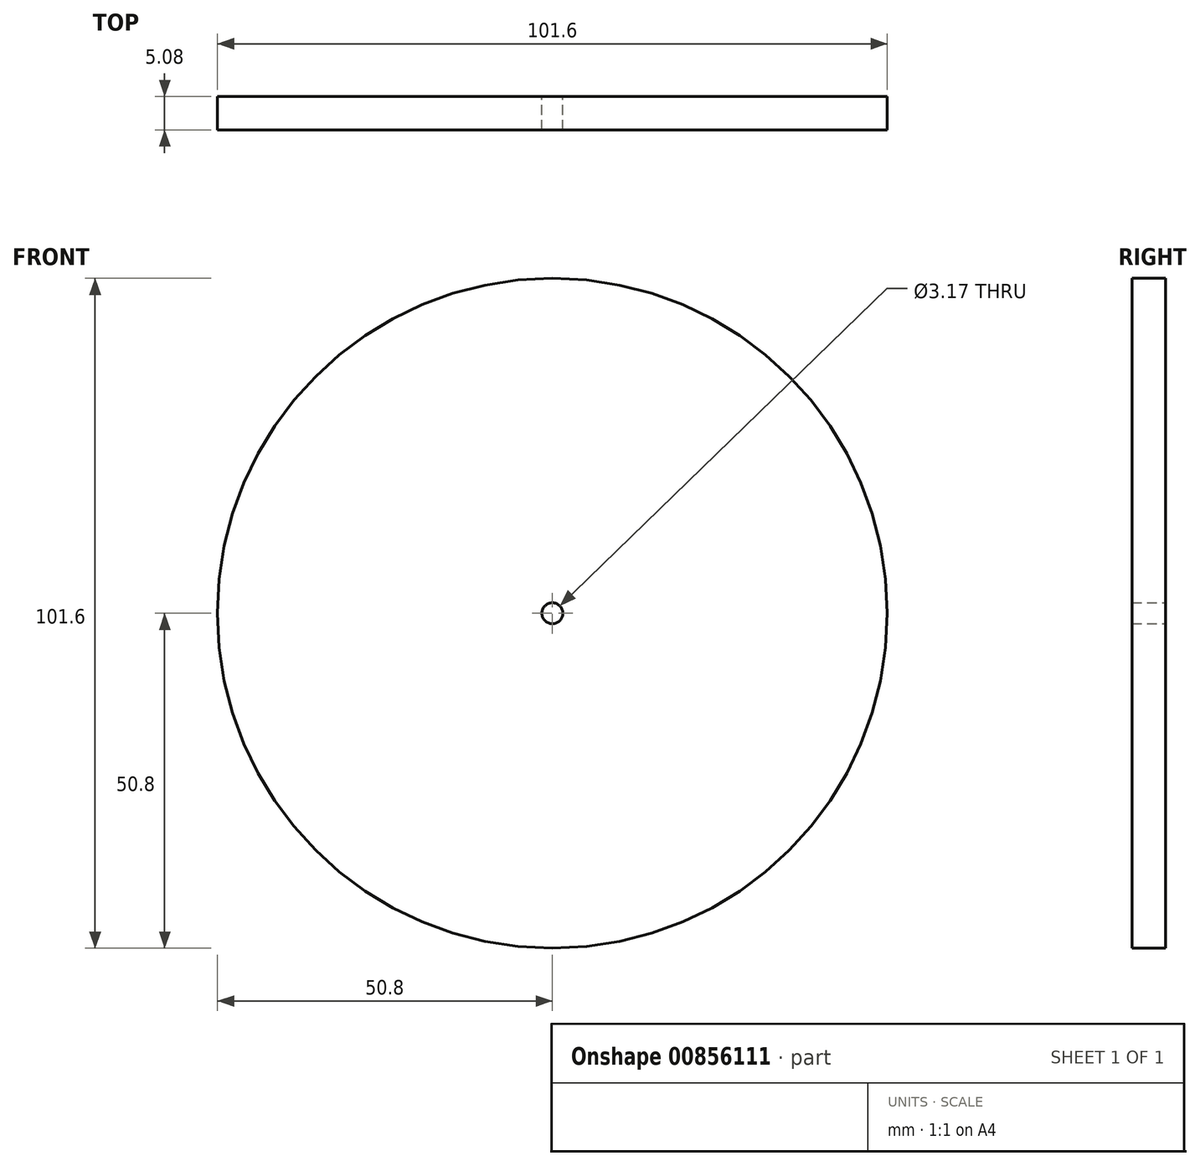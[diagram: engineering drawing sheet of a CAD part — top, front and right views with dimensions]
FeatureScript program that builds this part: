
annotation { "Feature Type Name" : "Feature", "Feature Type Description" : "" }
export const myFeature = defineFeature(function(context is Context, id is Id, definition is map)
    precondition{}
    {
        {
            var Q0;
            Q0=qCreatedBy(makeId("Front.planeOp"),FACE);
            var sketch = newSketch(context, id + "F0", { "sketchPlane" : qUnion([Q0])});
            skCircle(sketch, "E0", {"center": v(0, 0) * mm, "radius": 50.8 * mm});
            skCircle(sketch, "E1", {"center": v(0, 0) * mm, "radius": 1.59 * mm});
            skSolve(sketch);
        }
        {
            var Q0;
            Q0 = qSketchRegion(id + "F0", true);
            extrude(context, id + "F1", {"entities" : qUnion([Q0]), "depth" : 5.08 * mm, "offsetDistance" : 25.4 * mm});
        }
    });
